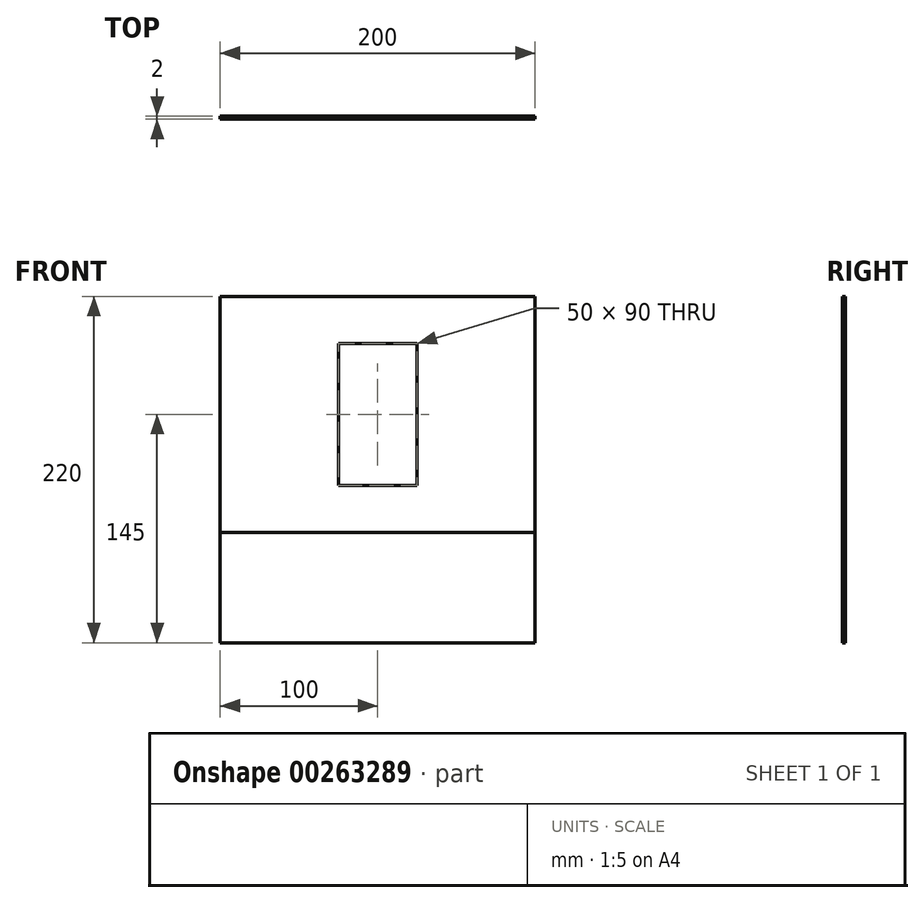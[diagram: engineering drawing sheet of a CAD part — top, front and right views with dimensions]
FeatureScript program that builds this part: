
annotation { "Feature Type Name" : "Feature", "Feature Type Description" : "" }
export const myFeature = defineFeature(function(context is Context, id is Id, definition is map)
    precondition{}
    {
        {
            var Q0;
            Q0=qCreatedBy(makeId("Front.planeOp"),FACE);
            var sketch = newSketch(context, id + "F0", { "sketchPlane" : qUnion([Q0])});
            skLineSegment(sketch, "E0.bottom", {"start": v(100, -75) * mm, "end": v(-100, -75) * mm});
            skLineSegment(sketch, "E0.top", {"start": v(100, 75) * mm, "end": v(-100, 75) * mm});
            skLineSegment(sketch, "E0.left", {"start": v(100, -75) * mm, "end": v(100, 75) * mm});
            skLineSegment(sketch, "E0.right", {"start": v(-100, -75) * mm, "end": v(-100, 75) * mm});
            skPoint(sketch, "E0.middle", {"position": v(0, 0) * mm});
            skSolve(sketch);
        }
        {
            var Q0;
            Q0 = qSketchRegion(id + "F0", true);
            extrude(context, id + "F1", {"entities" : qUnion([Q0]), "depth" : 2 * mm});
        }
        {
            var Q0;
            Q0=makeQuery(id+"F1.opExtrude","CAP_FACE",FACE,{"disambiguationData":[OSD([sQuery(id+"F0.wireOp",EDGE,"E0.bottom"),sQuery(id+"F0.wireOp",EDGE,"E0.top"),sQuery(id+"F0.wireOp",EDGE,"E0.left"),sQuery(id+"F0.wireOp",EDGE,"E0.right")])],"isStart":false});
            var sketch = newSketch(context, id + "F2", { "sketchPlane" : qUnion([Q0])});
            skLineSegment(sketch, "E1.bottom", {"start": v(25, -45) * mm, "end": v(-25, -45) * mm});
            skLineSegment(sketch, "E1.top", {"start": v(25, 45) * mm, "end": v(-25, 45) * mm});
            skLineSegment(sketch, "E1.left", {"start": v(25, -45) * mm, "end": v(25, 45) * mm});
            skLineSegment(sketch, "E1.right", {"start": v(-25, -45) * mm, "end": v(-25, 45) * mm});
            skPoint(sketch, "E1.middle", {"position": v(0, 0) * mm});
            skSolve(sketch);
        }
        {
            var Q0;
            Q0 = qSketchRegion(id + "F2", true);
            extrude(context, id + "F3", {"entities" : qUnion([Q0]), "operationType" : NewBodyOperationType.REMOVE, "oppositeDirection" : true, "depth" : 2 * mm});
        }
        {
            var Q0;
            Q0=makeQuery(id+"F1.opExtrude","CAP_FACE",FACE,{"disambiguationData":[OSD([sQuery(id+"F0.wireOp",EDGE,"E0.bottom"),sQuery(id+"F0.wireOp",EDGE,"E0.top"),sQuery(id+"F0.wireOp",EDGE,"E0.left"),sQuery(id+"F0.wireOp",EDGE,"E0.right")])],"isStart":false});
            var sketch = newSketch(context, id + "F4", { "sketchPlane" : qUnion([Q0])});
            skLineSegment(sketch, "E2.bottom", {"start": v(-100, -75) * mm, "end": v(100, -75) * mm});
            skLineSegment(sketch, "E2.top", {"start": v(-100, -145) * mm, "end": v(100, -145) * mm});
            skLineSegment(sketch, "E2.left", {"start": v(-100, -75) * mm, "end": v(-100, -145) * mm});
            skLineSegment(sketch, "E2.right", {"start": v(100, -75) * mm, "end": v(100, -145) * mm});
            skSolve(sketch);
        }
        {
            var Q0;
            Q0 = qSketchRegion(id + "F4", true);
            extrude(context, id + "F5", {"entities" : qUnion([Q0]), "oppositeDirection" : true, "depth" : 2 * mm});
        }
    });
